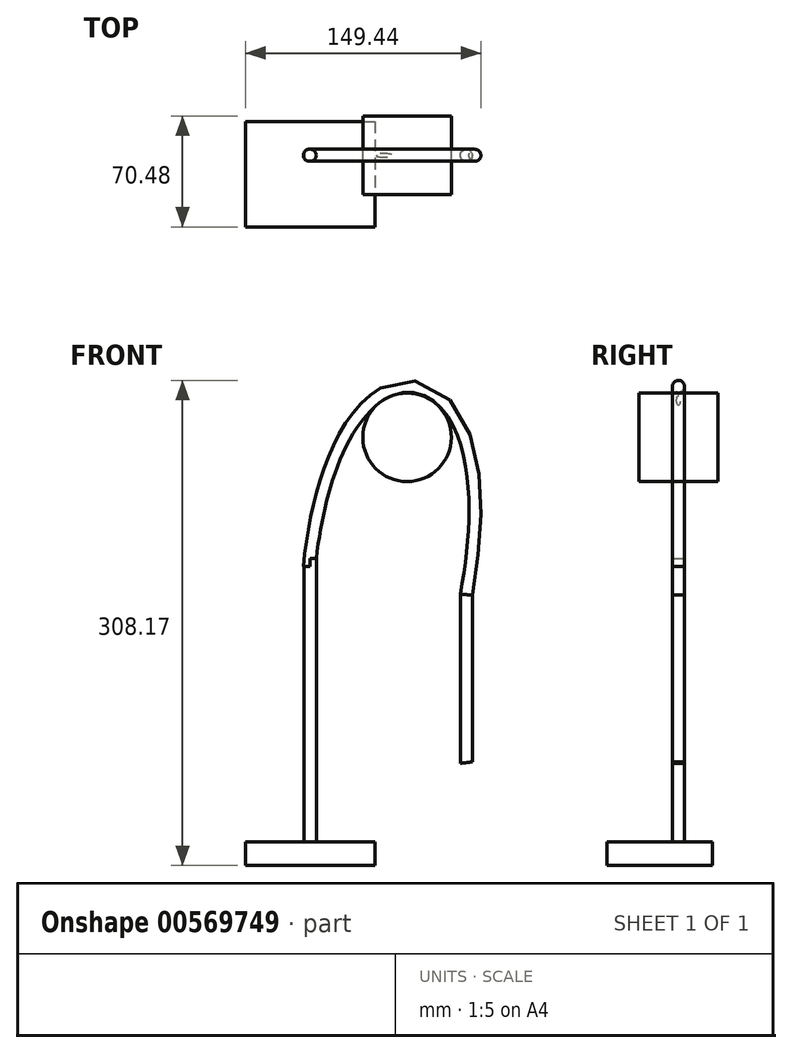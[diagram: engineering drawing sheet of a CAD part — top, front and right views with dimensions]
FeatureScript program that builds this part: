
annotation { "Feature Type Name" : "Feature", "Feature Type Description" : "" }
export const myFeature = defineFeature(function(context is Context, id is Id, definition is map)
    precondition{}
    {
        {
            var Q0;
            Q0=qCreatedBy(makeId("Top.planeOp"),FACE);
            var sketch = newSketch(context, id + "F0", { "sketchPlane" : qUnion([Q0])});
            skLineSegment(sketch, "E0.bottom", {"start": v(-60.25, 21.52) * mm, "end": v(21.87, 21.52) * mm});
            skLineSegment(sketch, "E0.top", {"start": v(-60.25, -45.48) * mm, "end": v(21.87, -45.48) * mm});
            skLineSegment(sketch, "E0.left", {"start": v(-60.25, 21.52) * mm, "end": v(-60.25, -45.48) * mm});
            skLineSegment(sketch, "E0.right", {"start": v(21.87, 21.52) * mm, "end": v(21.87, -45.48) * mm});
            skSolve(sketch);
        }
        {
            var Q0;
            Q0=makeQuery(id+"F0.imprint","IMPRINT",FACE,{"disambiguationData":[TD([[makeQuery(id+"F0.imprint","IMPRINT",EDGE,{"derivedFrom":sQuery(id+"F0.wireOp",EDGE,"E0.bottom")}),-1.0]])]});
            extrude(context, id + "F1", {"entities" : qUnion([Q0]), "depth" : 15 * mm, "offsetDistance" : 25 * mm});
        }
        {
            var Q0;
            Q0=makeQuery(id+"F1.opExtrude","CAP_FACE",FACE,{"disambiguationData":[OSD([sQuery(id+"F0.wireOp",EDGE,"E0.bottom"),sQuery(id+"F0.wireOp",EDGE,"E0.top"),sQuery(id+"F0.wireOp",EDGE,"E0.left"),sQuery(id+"F0.wireOp",EDGE,"E0.right")])],"isStart":false});
            var sketch = newSketch(context, id + "F2", { "sketchPlane" : qUnion([Q0])});
            skPoint(sketch, "E1.centerSnap0", {"position": v(-60.25, -11.98) * mm});
            skPoint(sketch, "E1.centerSnap1", {"position": v(-19.2, 21.52) * mm});
            skCircle(sketch, "E2", {"center": v(-19.2, 0) * mm, "radius": 3.83 * mm});
            skSolve(sketch);
        }
        {
            var Q0;
            Q0=makeQuery(id+"F2.imprint","IMPRINT",FACE,{"disambiguationData":[TD([[makeQuery(id+"F2.imprint","IMPRINT",EDGE,{"derivedFrom":sQuery(id+"F2.wireOp",EDGE,"E2")}),1.0]])]});
            extrude(context, id + "F3", {"entities" : qUnion([Q0]), "operationType" : NewBodyOperationType.ADD, "depth" : 180 * mm, "offsetDistance" : 25 * mm});
        }
        {
            var Q0;
            Q0=qCreatedBy(makeId("Front.planeOp"),FACE);
            var sketch = newSketch(context, id + "F4", { "sketchPlane" : qUnion([Q0])});
            skFitSpline(sketch, "E3", {"points": [v(-17.08, 189.98) * mm, v(41.24, 301.65) * mm, v(77.26, 172.33) * mm], "startDerivative": vector(44.02, 431) * mm, "endDerivative": vector(-102.17, -553.68) * mm});
            skLineSegment(sketch, "E4", {"start": v(77.26, 172.33) * mm, "end": v(77.26, 65.08) * mm});
            skSolve(sketch);
        }
        {
            var Q0;
            Q0=makeQuery(id+"F3.opExtrude","CAP_FACE",FACE,{"disambiguationData":[OSD([sQuery(id+"F2.wireOp",EDGE,"E2")])],"isStart":false});
            var Q1;
            Q1=sQuery(id+"F4.wireOp",EDGE,"E3");
            var Q2;
            Q2=sQuery(id+"F4.wireOp",EDGE,"E4");
            sweep(context, id + "F5", {"operationType" : NewBodyOperationType.ADD, "profiles" : qUnion([Q0]), "path" : qUnion([Q1, Q2])});
        }
        {
            var Q0;
            Q0=makeQuery(id+"F5.opSweep","CAP_FACE",FACE,{"disambiguationData":[OSD([sQuery(id+"F2.wireOp",EDGE,"E2"),sQuery(id+"F4.wireOp",VERTEX,"E3.end")])],"isStart":false});
            var sketch = newSketch(context, id + "F6", { "sketchPlane" : qUnion([Q0])});
            skCircle(sketch, "E5", {"center": v(85.58, 0) * mm, "radius": 3.9 * mm});
            skSolve(sketch);
        }
        {
            var Q0;
            Q0=qCreatedBy(makeId("Front.planeOp"),FACE);
            var sketch = newSketch(context, id + "F7", { "sketchPlane" : qUnion([Q0])});
            skCircle(sketch, "E6", {"center": v(42.28, 271.99) * mm, "radius": 28.11 * mm});
            skSolve(sketch);
        }
        {
            var Q0;
            Q0=makeQuery(id+"F7.imprint","IMPRINT",FACE,{"disambiguationData":[TD([[makeQuery(id+"F7.imprint","IMPRINT",EDGE,{"derivedFrom":sQuery(id+"F7.wireOp",EDGE,"E6")}),1.0]])]});
            extrude(context, id + "F8", {"entities" : qUnion([Q0]), "depth" : 25 * mm, "offsetDistance" : 25 * mm});
        }
        {
            var Q0;
            Q0=makeQuery(id+"F8.opExtrude","CAP_FACE",FACE,{"disambiguationData":[OSD([sQuery(id+"F7.wireOp",EDGE,"E6")])],"isStart":true});
            extrude(context, id + "F9", {"entities" : qUnion([Q0]), "operationType" : NewBodyOperationType.ADD, "depth" : 25 * mm, "offsetDistance" : 25 * mm});
        }
    });
